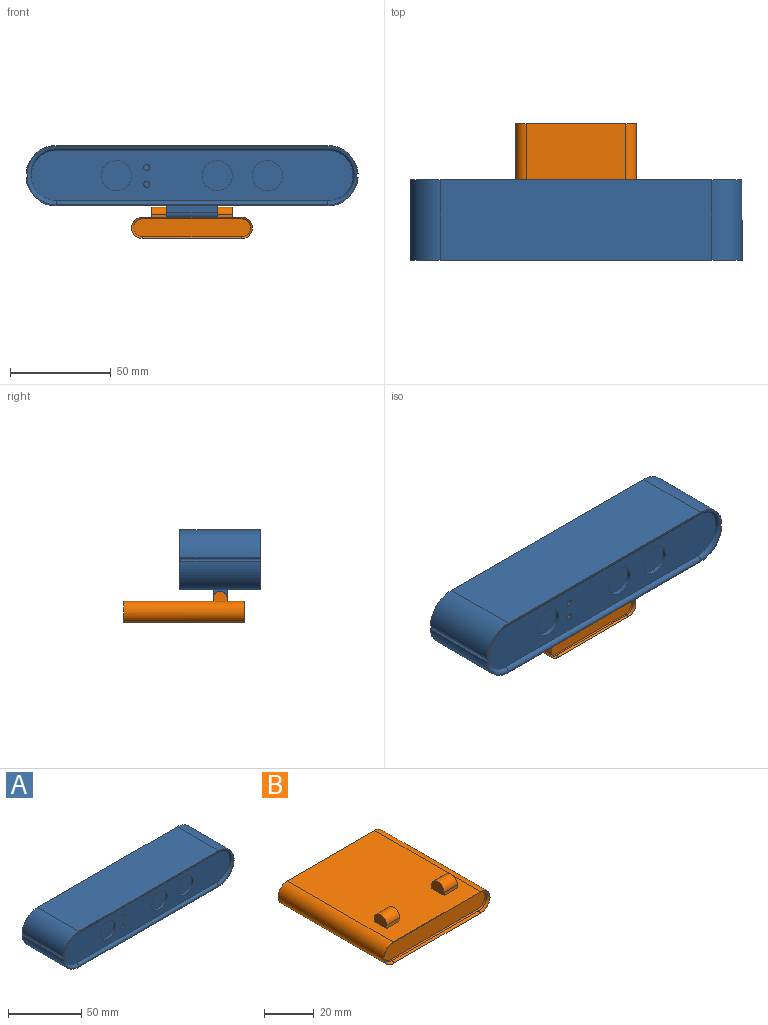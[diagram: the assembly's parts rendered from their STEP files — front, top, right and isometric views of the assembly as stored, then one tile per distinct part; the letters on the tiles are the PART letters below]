
ASSEMBLY  parts=2 mates=1
PART A: 37 faces, bbox 169.5x40x39.2 mm
  f0: plane 164.93x14.15mm, normal (0,1,0), area 89.7mm2, adj f3,f6,f8,f22,f23,f33,f34,f36
  f1: plane 164.93x14.15mm, normal (0,-1,0), area 89.7mm2, adj f3,f6,f8,f22,f23,f29,f30,f32
  f2: cylinder r=15mm len=40mm, axis (0,-1,0), area 902.5mm2, adj f4,f5,f7,f23
  f3: cylinder r=15mm len=40mm, axis (0,-1,0), area 902.5mm2, adj f0,f1,f6,f22
  f4: plane 164.93x14.15mm, normal (0,1,0), area 89.7mm2, adj f2,f7,f9,f22,f23,f33,f35,f36
  f5: plane 164.93x14.15mm, normal (0,-1,0), area 89.7mm2, adj f2,f7,f9,f22,f23,f29,f31,f32
  f6: plane 135x40mm, normal (0,0,-1), area 5225mm2, adj f0,f1,f3,f8,f24,f25,f26,f27
  f7: plane 135x40mm, normal (0,0,1), area 5400mm2, adj f2,f4,f5,f9
  f8: cylinder r=15mm len=40mm, axis (0,-1,0), area 902.5mm2, adj f0,f1,f6,f23
  f9: cylinder r=15mm len=40mm, axis (0,-1,0), area 902.5mm2, adj f4,f5,f7,f22
  f10: plane 160x25mm, normal (0,-1,0), area 3321.6mm2, adj f12,f14,f16,f18,f20,f29,f30,f31
  f11: plane 160x25mm, normal (0,1,0), area 3865.9mm2, adj f33,f34,f35,f36
  f12: cylinder r=1.5mm len=3mm, axis (0,-1,0), area 18.8mm2, adj f10,f13
  f13: plane 3x3mm, normal (0,-1,0), area 7.1mm2, adj f12
  f14: cylinder r=1.5mm len=3mm, axis (0,-1,0), area 18.8mm2, adj f10,f15
  f15: plane 3x3mm, normal (0,-1,0), area 7.1mm2, adj f14
  f16: cylinder r=7.5mm len=15mm, axis (0,-1,0), area 94.2mm2, adj f10,f17
  f17: plane 15x15mm, normal (0,-1,0), area 176.7mm2, adj f16
  f18: cylinder r=7.5mm len=15mm, axis (0,-1,0), area 94.2mm2, adj f10,f19
  f19: plane 15x15mm, normal (0,-1,0), area 176.7mm2, adj f18
  f20: cylinder r=7.5mm len=15mm, axis (0,-1,0), area 94.2mm2, adj f10,f21
  f21: plane 15x15mm, normal (0,-1,0), area 176.7mm2, adj f20
  f22: cylinder r=1mm len=40mm, axis (0,-1,0), area 122.9mm2, adj f0,f1,f3,f4,f5,f9,f29,f36
  f23: cylinder r=1mm len=40mm, axis (0,-1,0), area 122.9mm2, adj f0,f1,f2,f4,f5,f8,f32,f33
  f24: plane 25x3.5mm, normal (0,1,0), area 87.5mm2, adj f6,f25,f27,f28
  f25: plane 7x7mm, normal (1,0,0), area 43.7mm2, adj f6,f24,f26,f28
  f26: plane 25x3.5mm, normal (0,-1,0), area 87.5mm2, adj f6,f25,f27,f28
  f27: plane 7x7mm, normal (-1,0,0), area 43.7mm2, adj f6,f24,f26,f28
  f28: cylinder r=3.5mm len=25mm, axis (-1,0,0), area 274.9mm2, adj f24,f25,f26,f27
  f29: torus R=14.5mm, axis (0,-1,0), area 129.9mm2, adj f1,f5,f10,f22,f30,f31
  f30: cylinder r=2mm len=135mm, axis (-1,0,0), area 424.1mm2, adj f1,f10,f29,f32
  f31: cylinder r=2mm len=135mm, axis (1,0,0), area 424.1mm2, adj f5,f10,f29,f32
  f32: torus R=14.5mm, axis (0,-1,0), area 129.9mm2, adj f1,f5,f10,f23,f30,f31
  f33: torus R=14.5mm, axis (0,-1,0), area 129.9mm2, adj f0,f4,f11,f23,f34,f35
  f34: cylinder r=2mm len=135mm, axis (-1,0,0), area 424.1mm2, adj f0,f11,f33,f36
  f35: cylinder r=2mm len=135mm, axis (1,0,0), area 424.1mm2, adj f4,f11,f33,f36
  f36: torus R=14.5mm, axis (0,-1,0), area 129.9mm2, adj f0,f4,f11,f22,f34,f35
PART B: 26 faces, bbox 62.4x60x17 mm
  f0: plane 7.5x1.5mm, normal (0,-1,0), area 11.2mm2, adj f3,f21,f22,f24
  f1: plane 7.5x1.5mm, normal (0,1,0), area 11.2mm2, adj f3,f21,f22,f24
  f2: plane 59.97x49.5mm, normal (0,0,-1), area 2889.9mm2, adj f4,f5,f6,f12,f13,f15,f16
  f3: plane 59.97x49.5mm, normal (0,0,1), area 2863.4mm2, adj f0,f1,f4,f5,f6,f12,f14,f15
  f4: plane 60x10.5mm, normal (0,1,0), area 606.3mm2, adj f2,f3,f5,f6
  f5: cylinder r=5.25mm len=60mm, axis (0,-1,0), area 989.4mm2, adj f2,f3,f4,f15
  f6: cylinder r=5.25mm len=60mm, axis (0,-1,0), area 989.4mm2, adj f2,f3,f4,f12
  f7: plane 49x1mm, normal (0,0,1), area 49mm2, adj f8,f10,f11,f13
  f8: cylinder r=4.5mm len=9mm, axis (0,-1,0), area 14.1mm2, adj f7,f9,f11,f15
  f9: plane 49x1mm, normal (0,0,-1), area 49mm2, adj f8,f10,f11,f14
  f10: cylinder r=4.5mm len=9mm, axis (0,-1,0), area 14.1mm2, adj f7,f9,f11,f12
  f11: plane 58x9mm, normal (0,-1,0), area 504.6mm2, adj f7,f8,f9,f10
  f12: torus R=5.5mm, axis (0,-1,0), area 22.4mm2, adj f2,f3,f6,f10,f13,f14
  f13: cylinder r=1mm len=49mm, axis (-1,0,0), area 64.6mm2, adj f2,f7,f12,f15
  f14: cylinder r=1mm len=49mm, axis (1,0,0), area 64.6mm2, adj f3,f9,f12,f15
  f15: torus R=5.5mm, axis (0,-1,0), area 22.4mm2, adj f2,f3,f5,f8,f13,f14
  f16: cylinder r=5mm len=10mm, axis (0,0,-1), area 157.1mm2, adj f2,f17
  f17: plane 10x10mm, normal (0,0,-1), area 78.5mm2, adj f16
  f18: plane 7.5x1.5mm, normal (0,-1,0), area 11.2mm2, adj f3,f19,f23,f25
  f19: plane 7x5mm, normal (1,0,0), area 29.7mm2, adj f3,f18,f20,f25
  f20: plane 7.5x1.5mm, normal (0,1,0), area 11.2mm2, adj f3,f19,f23,f25
  f21: plane 7x5mm, normal (-1,0,0), area 29.7mm2, adj f0,f1,f3,f24
  f22: plane 7x5mm, normal (1,0,0), area 29.7mm2, adj f0,f1,f3,f24
  f23: plane 7x5mm, normal (-1,0,0), area 29.7mm2, adj f3,f18,f20,f25
  f24: cylinder r=3.5mm len=7.5mm, axis (-1,0,0), area 82.5mm2, adj f0,f1,f21,f22
  f25: cylinder r=3.5mm len=7.5mm, axis (-1,0,0), area 82.5mm2, adj f18,f19,f20,f23
PLACE A t=(0,-17.97,-8.15)mm
PLACE B t=(0,0,-34.1)mm fixed
MATE revolute A.f28 <-> B.f23  axis (1,0,0) through (12.5,-17.97,-26.65)mm
